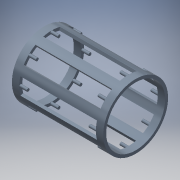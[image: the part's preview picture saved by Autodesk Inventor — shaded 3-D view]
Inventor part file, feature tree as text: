
AUTODESK INVENTOR PART (.ipt)
format: ipt  version: 2018 (Build 220112000, 112)  size: 178,688 bytes
history: native  units: in
note: dims shown in document units (in); Inventor stores cm internally (conversion verified against a paired STEP export)
features: sketch x3, revolve x2, extrude x1, mirror x1, pattern_circular x1
ambient origin geometry x8: Origin, YZ Plane, XZ Plane, XY Plane, X Axis, Y Axis, Z Axis, Center Point
bodies: Solid1 (feature_tree)
feature tree (8):
  revolve  "Revolution1"  Angle=90.0deg
  revolve  "Revolution2"  [1 undecoded]
  extrude  "Extrusion1"  Depth=10.0in
  mirror  "Mirror1"
  pattern_circular  "Circular Pattern1"  [2 undecoded]
  sketch  "Sketch1"  dims[d4=4.0in d5=90.0deg]
  sketch  "Sketch2"  dims[d7=45.0deg d8=10.0in d9=0.0in]
  sketch  "Sketch3"  dims[d10=2.3622in d11=360.0deg d16=10.0in d18=42.0in d19=124.0in]
note: 3 required parameter values undecoded (feature->parameter linkage not recoverable at this tier; creation-order binding heuristic only, values carry confidence <= 0.55)